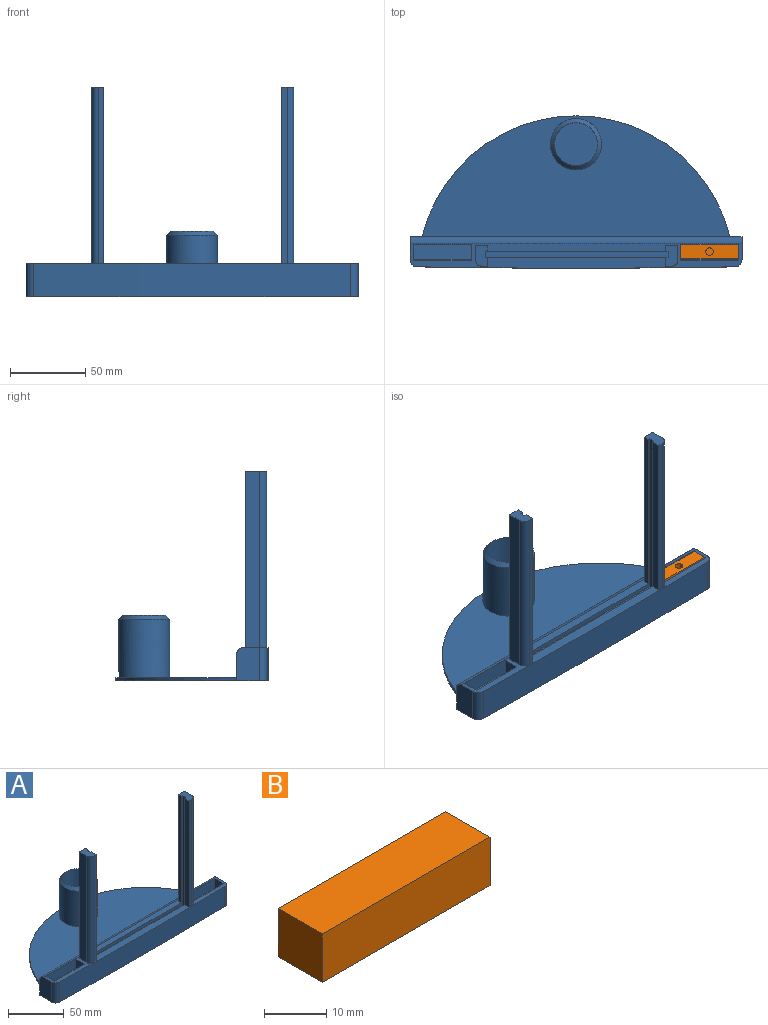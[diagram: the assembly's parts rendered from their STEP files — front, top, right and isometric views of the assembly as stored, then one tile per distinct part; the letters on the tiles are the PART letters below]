
ASSEMBLY  parts=2 mates=1
PART A: 142 faces, bbox 220x101x139.1 mm
  f0: plane 117.1x3.5mm, normal (0,-1,0), area 409.9mm2, adj f2,f12,f16,f134
  f1: plane 220x17.5mm, normal (0,1,0), area 3310.1mm2, adj f3,f5,f6,f32,f33,f42,f43,f44
  f2: plane 220x16.5mm, normal (0,0,1), area 2044mm2, adj f0,f3,f4,f5,f8,f10,f12,f13
  f3: plane 22x15.09mm, normal (-1,0,0), area 327.6mm2, adj f1,f2,f6,f136,f140
  f4: plane 117.1x3.5mm, normal (0,-1,0), area 409.9mm2, adj f2,f17,f21,f135
  f5: plane 22x15.09mm, normal (1,0,0), area 327.6mm2, adj f1,f2,f6,f136,f141
  f6: plane 220x101mm, normal (0,0,-1), area 16656.3mm2, adj f1,f3,f5,f32,f137,f140,f141
  f7: plane 120.1x3.85mm, normal (1,0,0), area 462.4mm2, adj f8,f10,f11,f16
  f8: plane 121x120.1mm, normal (0,1,0), area 714.3mm2, adj f2,f7,f9,f11,f12,f16,f17,f21
  f9: plane 120.1x3.85mm, normal (-1,0,0), area 462.4mm2, adj f8,f10,f11,f21
  f10: plane 121x120.1mm, normal (0,-1,0), area 714.3mm2, adj f2,f7,f9,f11,f13,f16,f20,f21
  f11: plane 121x3.85mm, normal (0,0,1), area 465.8mm2, adj f7,f8,f9,f10
  f12: plane 117.1x6mm, normal (1,0,0), area 702.6mm2, adj f0,f2,f8,f16
  f13: plane 117.1x3.95mm, normal (1,0,0), area 462.5mm2, adj f2,f10,f14,f16
  f14: plane 117.1x8mm, normal (0,1,0), area 936.8mm2, adj f2,f13,f15,f16
  f15: plane 117.1x9.3mm, normal (-1,0,0), area 1089mm2, adj f2,f14,f16,f134
  f16: plane 13.8x8mm, normal (0,0,1), area 100.3mm2, adj f0,f7,f8,f10,f12,f13,f14,f15
  f17: plane 117.1x6mm, normal (-1,0,0), area 702.6mm2, adj f2,f4,f8,f21
  f18: plane 117.1x9.3mm, normal (1,0,0), area 1089mm2, adj f2,f19,f21,f135
  f19: plane 117.1x8mm, normal (0,1,0), area 936.8mm2, adj f2,f18,f20,f21
  f20: plane 117.1x3.95mm, normal (-1,0,0), area 462.5mm2, adj f2,f10,f19,f21
  f21: plane 13.8x8mm, normal (0,0,1), area 100.3mm2, adj f4,f8,f9,f10,f17,f18,f19,f20
  f22: plane 38x10mm, normal (0,-1,0), area 380mm2, adj f2,f23,f25,f26
  f23: plane 11x10mm, normal (1,0,0), area 100.5mm2, adj f2,f22,f24,f26,f138
  f24: plane 38x9mm, normal (0,1,0), area 342mm2, adj f23,f25,f26,f138
  f25: plane 11x10mm, normal (-1,0,0), area 100.5mm2, adj f2,f22,f24,f26,f138
  f26: plane 38x10mm, normal (0,0,1), area 380mm2, adj f22,f23,f24,f25
  f27: plane 38x10mm, normal (0,-1,0), area 380mm2, adj f2,f28,f30,f31
  f28: plane 11x10mm, normal (1,0,0), area 100.5mm2, adj f2,f27,f29,f31,f139
  f29: plane 38x9mm, normal (0,1,0), area 342mm2, adj f28,f30,f31,f139
  f30: plane 11x10mm, normal (-1,0,0), area 100.5mm2, adj f2,f27,f29,f31,f139
  f31: plane 38x10mm, normal (0,0,1), area 380mm2, adj f27,f28,f29,f30
  f32: cylinder r=105.02mm len=204mm, axis (0,0,-1), area 558.8mm2, adj f1,f6,f33
  f33: plane 204x80mm, normal (0,0,1), area 11212mm2, adj f1,f32,f34
  f34: cylinder r=17mm len=39mm, axis (0,0,-1), area 4140.9mm2, adj f33,f37,f38,f39,f40,f41
  f35: cylinder r=14.3mm len=41.7mm, axis (0,0,-1), area 3721.8mm2, adj f36,f37,f38,f39,f40,f41
  f36: plane 28.6x28.6mm, normal (0,0,1), area 642.4mm2, adj f35
  f37: plane 3.8x2.76mm, normal (-1,0,0), area 10.5mm2, adj f34,f35,f38,f40
  f38: plane 6.5x3.08mm, normal (0,0,-1), area 17.7mm2, adj f34,f35,f37,f39
  f39: plane 3.8x2.76mm, normal (1,0,0), area 10.5mm2, adj f34,f35,f38,f40
  f40: plane 6.5x3.08mm, normal (0,0,1), area 17.7mm2, adj f34,f35,f37,f39
  f41: cone r=14mm half-angle=45deg, axis (0,0,-1), area 375.5mm2, adj f34,f35
  f42: plane 3.5x1.59mm, normal (0,0,-1), area 5.6mm2, adj f1,f43,f58,f59
  f43: plane 5.3x3.5mm, normal (-0.93,0,0.37), area 20mm2, adj f1,f42,f44,f59
  f44: plane 3.5x0.26mm, normal (-0.95,0,-0.31), area 1mm2, adj f1,f43,f45,f59
  f45: extruded ~3.5x0.71mm, area 3mm2, adj f1,f44,f46,f59
  f46: extruded ~3.5x0.68mm, area 2.6mm2, adj f1,f45,f47,f59
  f47: extruded ~3.5x0.57mm, area 2mm2, adj f1,f46,f48,f59
  f48: plane 3.5x1.15mm, normal (-1,0,0), area 4mm2, adj f1,f47,f49,f59
  f49: extruded ~3.5x0.74mm, area 2.6mm2, adj f1,f48,f50,f59
  f50: extruded ~3.5x1.34mm, area 5mm2, adj f1,f49,f51,f59
  f51: extruded ~3.5x1.25mm, area 5.4mm2, adj f1,f50,f52,f59
  f52: plane 6.02x3.5mm, normal (0.94,0,0.35), area 22.5mm2, adj f1,f51,f53,f59
  f53: plane 3.5x1.56mm, normal (0,0,-1), area 5.5mm2, adj f1,f52,f54,f59
  f54: plane 3.5x3mm, normal (-0.95,0,-0.31), area 11.1mm2, adj f1,f53,f55,f59
  f55: extruded ~3.5x0.93mm, area 3.3mm2, adj f1,f54,f56,f59
  f56: plane 3.5x0.03mm, normal (0,0,-1), area 0.1mm2, adj f1,f55,f57,f59
  f57: extruded ~3.5x0.93mm, area 3.3mm2, adj f1,f56,f58,f59
  f58: plane 3.5x3mm, normal (0.95,0,-0.32), area 11.1mm2, adj f1,f42,f57,f59
  f59: plane 7.68x5.56mm, normal (0,1,0), area 18.6mm2, adj f42,f43,f44,f45,f46,f47,f48,f49
  f60: extruded ~3.5x2.25mm, area 12mm2, adj f61,f71,f72,f132
  f61: extruded ~3.5x2.29mm, area 12.6mm2, adj f60,f62,f72,f132
  f62: plane 3.5x0.63mm, normal (0,0,-1), area 2.2mm2, adj f61,f63,f72,f132
  f63: plane 4.54x3.5mm, normal (1,0,0), area 15.9mm2, adj f62,f71,f72,f132
  f64: extruded ~3.5x2.64mm, area 10.1mm2, adj f1,f65,f70,f72
  f65: extruded ~3.5x2.52mm, area 9.7mm2, adj f1,f64,f66,f72
  f66: extruded ~3.5x2.65mm, area 10.1mm2, adj f1,f65,f67,f72
  f67: plane 3.5x2.19mm, normal (0,0,-1), area 7.7mm2, adj f1,f66,f68,f72
  f68: plane 6.98x3.5mm, normal (-1,0,0), area 24.4mm2, adj f1,f67,f69,f72
  f69: plane 3.5x1.98mm, normal (0,0,1), area 6.9mm2, adj f1,f68,f70,f72
  f70: extruded ~3.5x2.83mm, area 10.7mm2, adj f1,f64,f69,f72
  f71: plane 3.5x0.79mm, normal (0,0,1), area 2.8mm2, adj f60,f63,f72,f132
  f72: plane 6.98x5.79mm, normal (0,1,0), area 24.8mm2, adj f60,f61,f62,f63,f64,f65,f66,f67
  f73: extruded ~3.5x1.72mm, area 6.7mm2, adj f1,f74,f88,f89
  f74: extruded ~3.5x1.63mm, area 6.4mm2, adj f1,f73,f75,f89
  f75: extruded ~3.5x1.93mm, area 7.2mm2, adj f1,f74,f76,f89
  f76: plane 3.5x2.23mm, normal (0,0,-1), area 7.8mm2, adj f1,f75,f77,f89
  f77: plane 6.98x3.5mm, normal (-1,0,0), area 24.4mm2, adj f1,f76,f78,f89
  f78: plane 3.5x1.48mm, normal (0,0,1), area 5.2mm2, adj f1,f77,f79,f89
  f79: plane 3.5x2.48mm, normal (1,0,0), area 8.7mm2, adj f1,f78,f80,f89
  f80: plane 3.5x0.63mm, normal (0,0,1), area 2.2mm2, adj f1,f79,f88,f89
  f81: plane 3.5x0.49mm, normal (0,0,-1), area 1.7mm2, adj f82,f87,f89,f90
  f82: plane 3.5x2.07mm, normal (1,0,0), area 7.2mm2, adj f81,f83,f89,f90
  f83: plane 3.5x0.67mm, normal (0,0,1), area 2.4mm2, adj f82,f84,f89,f90
  f84: extruded ~3.5x0.89mm, area 3.3mm2, adj f83,f85,f89,f90
  f85: extruded ~3.5x0.77mm, area 3mm2, adj f84,f86,f89,f90
  f86: extruded ~3.5x0.78mm, area 3.1mm2, adj f85,f87,f89,f90
  f87: extruded ~3.5x1.02mm, area 3.8mm2, adj f81,f86,f89,f90
  f88: extruded ~3.5x2mm, area 7.5mm2, adj f1,f73,f80,f89
  f89: plane 6.98x4.82mm, normal (0,1,0), area 19.9mm2, adj f73,f74,f75,f76,f77,f78,f79,f80
  f90: plane 2.07x1.85mm, normal (0,1,0), area 3.4mm2, adj f81,f82,f83,f84,f85,f86,f87
  f91: extruded ~3.5x2.25mm, area 12mm2, adj f92,f102,f103,f133
  f92: extruded ~3.5x2.29mm, area 12.6mm2, adj f91,f93,f103,f133
  f93: plane 3.5x0.63mm, normal (0,0,-1), area 2.2mm2, adj f92,f94,f103,f133
  f94: plane 4.54x3.5mm, normal (1,0,0), area 15.9mm2, adj f93,f102,f103,f133
  f95: extruded ~3.5x2.64mm, area 10.1mm2, adj f1,f96,f101,f103
  f96: extruded ~3.5x2.52mm, area 9.7mm2, adj f1,f95,f97,f103
  f97: extruded ~3.5x2.65mm, area 10.1mm2, adj f1,f96,f98,f103
  f98: plane 3.5x2.19mm, normal (0,0,-1), area 7.7mm2, adj f1,f97,f99,f103
  f99: plane 6.98x3.5mm, normal (-1,0,0), area 24.4mm2, adj f1,f98,f100,f103
  f100: plane 3.5x1.98mm, normal (0,0,1), area 6.9mm2, adj f1,f99,f101,f103
  f101: extruded ~3.5x2.83mm, area 10.7mm2, adj f1,f95,f100,f103
  f102: plane 3.5x0.79mm, normal (0,0,1), area 2.8mm2, adj f91,f94,f103,f133
  f103: plane 6.98x5.79mm, normal (0,1,0), area 24.8mm2, adj f91,f92,f93,f94,f95,f96,f97,f98
  f104: extruded ~3.5x1.11mm, area 4.2mm2, adj f1,f105,f130,f131
  f105: extruded ~3.5x1.22mm, area 5mm2, adj f1,f104,f106,f131
  f106: extruded ~3.5x1.71mm, area 6.3mm2, adj f1,f105,f107,f131
  f107: extruded ~3.5x2.28mm, area 8.5mm2, adj f1,f106,f108,f131
  f108: plane 3.5x1.02mm, normal (-0.83,0,0.56), area 4.3mm2, adj f1,f107,f109,f131
  f109: extruded ~3.5x0.79mm, area 3.1mm2, adj f1,f108,f110,f131
  f110: extruded ~3.5x0.7mm, area 2.5mm2, adj f1,f109,f111,f131
  f111: extruded ~3.5x0.99mm, area 5.1mm2, adj f1,f110,f112,f131
  f112: extruded ~3.5x0.73mm, area 3mm2, adj f1,f111,f113,f131
  f113: extruded ~3.5x1.19mm, area 4.3mm2, adj f1,f112,f114,f131
  f114: plane 3.5x0.54mm, normal (0,0,-1), area 1.9mm2, adj f1,f113,f115,f131
  f115: plane 3.5x1.13mm, normal (-1,0,0), area 4mm2, adj f1,f114,f116,f131
  f116: plane 3.5x0.53mm, normal (0,0,1), area 1.9mm2, adj f1,f115,f117,f131
  f117: extruded ~3.5x1.28mm, area 4.6mm2, adj f1,f116,f118,f131
  f118: extruded ~3.5x0.7mm, area 3mm2, adj f1,f117,f119,f131
  f119: extruded ~3.5x0.8mm, area 3.2mm2, adj f1,f118,f120,f131
  f120: extruded ~3.5x1.08mm, area 3.9mm2, adj f1,f119,f121,f131
  f121: extruded ~3.5x0.96mm, area 3.4mm2, adj f1,f120,f122,f131
  f122: extruded ~3.5x0.89mm, area 3.3mm2, adj f1,f121,f123,f131
  f123: plane 3.5x1.26mm, normal (-1,0,0), area 4.4mm2, adj f1,f122,f124,f131
  f124: extruded ~3.5x2.01mm, area 7.2mm2, adj f1,f123,f125,f131
  f125: extruded ~3.5x2.08mm, area 7.7mm2, adj f1,f124,f126,f131
  f126: extruded ~3.5x1.57mm, area 6.3mm2, adj f1,f125,f127,f131
  f127: extruded ~3.5x1.1mm, area 4.3mm2, adj f1,f126,f128,f131
  f128: extruded ~3.5x1.28mm, area 4.9mm2, adj f1,f127,f129,f131
  f129: plane 3.5x0.03mm, normal (1,0,0), area 0.1mm2, adj f1,f128,f130,f131
  f130: extruded ~3.5x1.11mm, area 4.5mm2, adj f1,f104,f129,f131
  f131: plane 7.17x4.83mm, normal (0,1,0), area 18.4mm2, adj f104,f105,f106,f107,f108,f109,f110,f111
  f132: plane 4.54x2.77mm, normal (0,1,0), area 11mm2, adj f60,f61,f62,f63,f71
  f133: plane 4.54x2.77mm, normal (0,1,0), area 11mm2, adj f91,f92,f93,f94,f102
  f134: cylinder r=4.5mm len=117.1mm, axis (0,0,1), area 827.7mm2, adj f0,f2,f15,f16
  f135: cylinder r=4.5mm len=117.1mm, axis (0,0,-1), area 827.7mm2, adj f2,f4,f18,f21
  f136: cylinder r=4.5mm len=220mm, axis (1,0,0), area 1555.1mm2, adj f1,f2,f3,f5
  f137: cylinder r=6050.5mm len=210.17mm, axis (0,0,-1), area 4624.1mm2, adj f2,f6,f140,f141
  f138: plane 38x1mm, normal (0,0.71,0.71), area 53.7mm2, adj f2,f23,f24,f25
  f139: plane 38x1mm, normal (0,0.71,0.71), area 53.7mm2, adj f2,f28,f29,f30
  f140: cylinder r=5mm len=22mm, axis (0,0,-1), area 170.9mm2, adj f2,f3,f6,f137
  f141: cylinder r=5mm len=22mm, axis (0,0,-1), area 170.9mm2, adj f2,f5,f6,f137
PART B: 8 faces, bbox 38x10x9.5 mm
  f0: plane 38x9.5mm, normal (0,1,0), area 341.4mm2, adj f1,f3,f4,f5,f6
  f1: plane 10x9.5mm, normal (-1,0,0), area 95mm2, adj f0,f2,f4,f5
  f2: plane 38x9.5mm, normal (0,-1,0), area 361mm2, adj f1,f3,f4,f5
  f3: plane 10x9.5mm, normal (1,0,0), area 95mm2, adj f0,f2,f4,f5
  f4: plane 38x10mm, normal (0,0,1), area 380mm2, adj f0,f1,f2,f3
  f5: plane 38x10mm, normal (0,0,-1), area 380mm2, adj f0,f1,f2,f3
  f6: cylinder r=2.5mm len=5mm, axis (0,1,0), area 78.5mm2, adj f0,f7
  f7: plane 5x5mm, normal (0,1,0), area 19.6mm2, adj f6
PLACE A t=(-40.51,22.45,31.23)mm
PLACE B rot(axis=(1,0,0),90deg) t=(-133.65,22.02,37.99)mm
MATE fastened B.f2 <-> A.f31  axis (0,0,-1) through (45.45,17.27,43.23)mm
